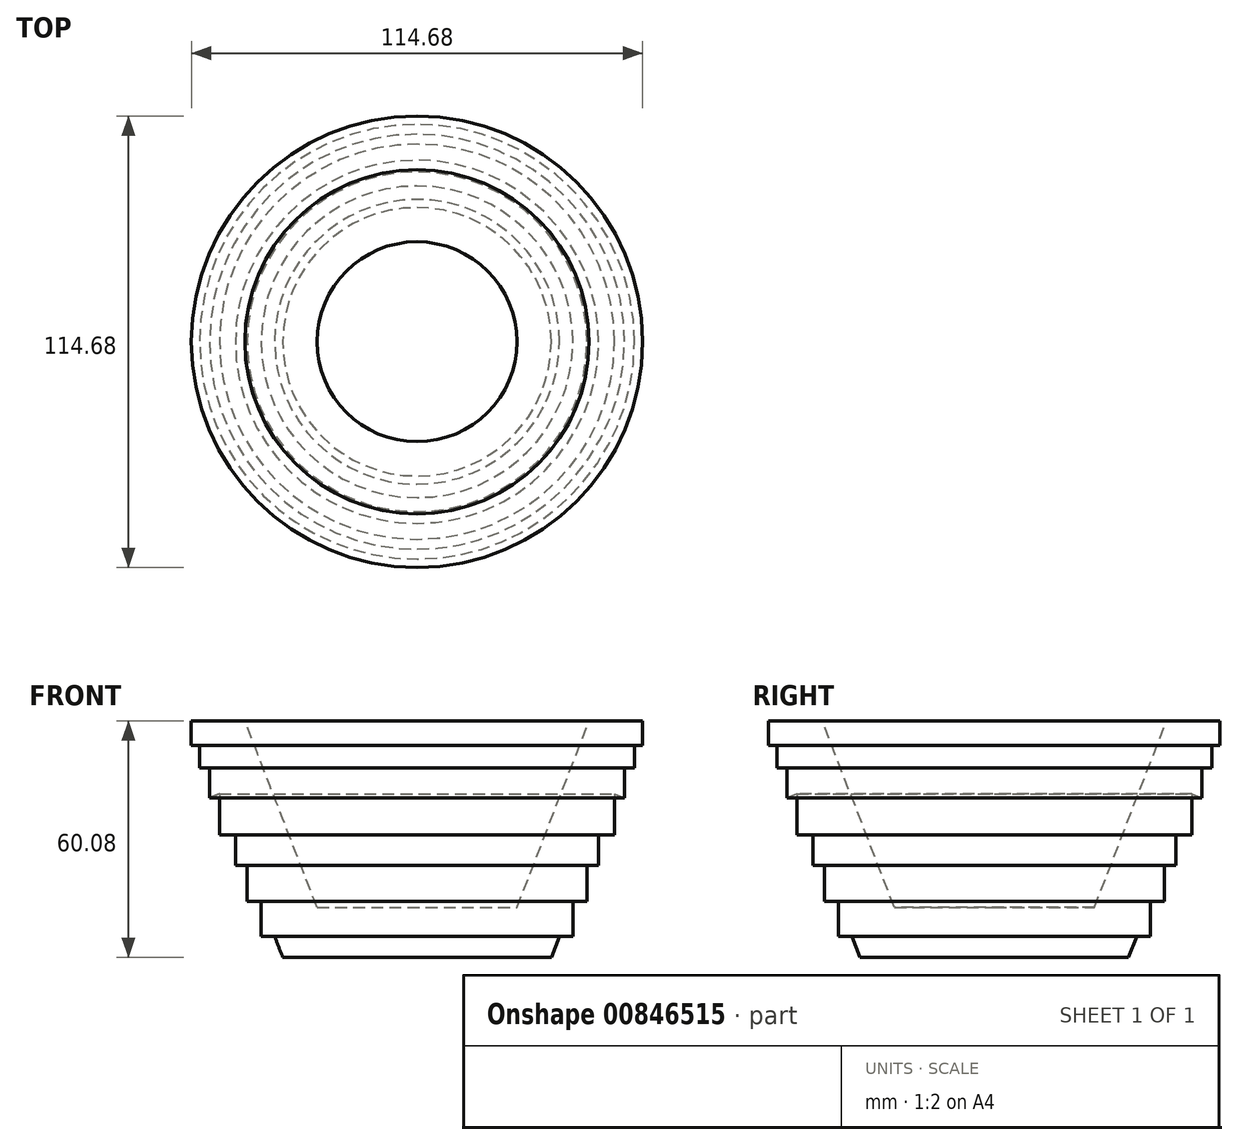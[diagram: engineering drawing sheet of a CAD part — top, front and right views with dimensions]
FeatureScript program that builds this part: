
annotation { "Feature Type Name" : "Feature", "Feature Type Description" : "" }
export const myFeature = defineFeature(function(context is Context, id is Id, definition is map)
    precondition{}
    {
        {
            var Q0;
            Q0=qCreatedBy(makeId("Front.planeOp"),FACE);
            var sketch = newSketch(context, id + "F0", { "sketchPlane" : qUnion([Q0])});
            skLineSegment(sketch, "E0", {"start": v(-55.22, -23.23) * mm, "end": v(-29.82, -23.23) * mm});
            skLineSegment(sketch, "E1", {"start": v(-29.82, -23.23) * mm, "end": v(-11.5, 24.15) * mm});
            skLineSegment(sketch, "E2.0", {"start": v(-21.12, -35.93) * mm, "end": v(2.12, 24.15) * mm});
            skLineSegment(sketch, "E2.1", {"start": v(-55.22, -35.93) * mm, "end": v(-21.12, -35.93) * mm});
            skLineSegment(sketch, "E3", {"start": v(-11.5, 24.15) * mm, "end": v(2.12, 24.15) * mm});
            skLineSegment(sketch, "E4", {"start": v(-55.22, -23.23) * mm, "end": v(-55.22, -35.93) * mm});
            skLineSegment(sketch, "E5", {"start": v(-55.22, -35.93) * mm, "end": v(-55.22, 24.15) * mm});
            skLineSegment(sketch, "E6", {"start": v(2.12, 24.15) * mm, "end": v(2.12, 17.96) * mm});
            skLineSegment(sketch, "E7", {"start": v(2.12, 17.96) * mm, "end": v(0, 17.96) * mm});
            skLineSegment(sketch, "E8", {"start": v(0, 17.96) * mm, "end": v(0, 12.2) * mm});
            skLineSegment(sketch, "E9", {"start": v(0, 12.2) * mm, "end": v(-2.5, 12.2) * mm});
            skLineSegment(sketch, "E10", {"start": v(-2.5, 12.2) * mm, "end": v(-2.5, 4.64) * mm});
            skLineSegment(sketch, "E11", {"start": v(-2.5, 4.64) * mm, "end": v(-5.05, 5.63) * mm});
            skLineSegment(sketch, "E12", {"start": v(-5.05, 5.63) * mm, "end": v(-5.05, -4.8) * mm});
            skLineSegment(sketch, "E13", {"start": v(-5.05, -4.8) * mm, "end": v(-9.08, -4.8) * mm});
            skLineSegment(sketch, "E14", {"start": v(-9.08, -4.8) * mm, "end": v(-9.08, -12.54) * mm});
            skLineSegment(sketch, "E15", {"start": v(-9.08, -12.54) * mm, "end": v(-12.07, -12.54) * mm});
            skLineSegment(sketch, "E16", {"start": v(-12.07, -12.54) * mm, "end": v(-12.07, -21.73) * mm});
            skLineSegment(sketch, "E17", {"start": v(-12.07, -21.73) * mm, "end": v(-15.63, -21.73) * mm});
            skLineSegment(sketch, "E18", {"start": v(-15.63, -21.73) * mm, "end": v(-15.63, -30.56) * mm});
            skLineSegment(sketch, "E19", {"start": v(-15.63, -30.56) * mm, "end": v(-19.04, -30.56) * mm});
            skSolve(sketch);
        }
        {
            var Q0;
            Q0 = qSketchRegion(id + "F0", true);
            var Q1;
            Q1=sQuery(id+"F0.wireOp",EDGE,"E5");
            revolve(context, id + "F1", {"surfaceOperationType" : NewSurfaceOperationType.NEW, "entities" : qUnion([Q0]), "axis" : qUnion([Q1]), "revolveType" : RevolveType.FULL});
        }
    });
